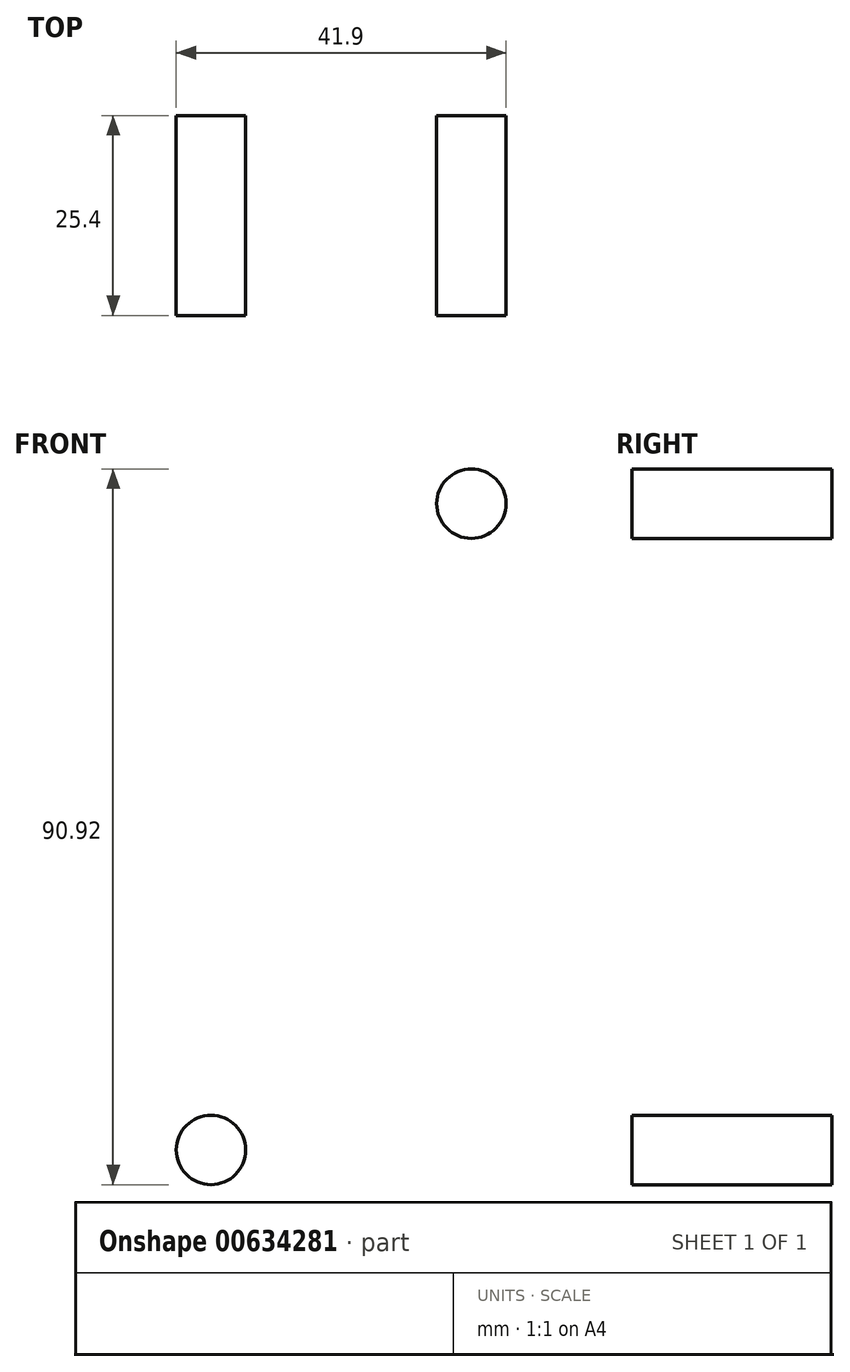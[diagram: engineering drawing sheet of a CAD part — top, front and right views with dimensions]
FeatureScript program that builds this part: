
annotation { "Feature Type Name" : "Feature", "Feature Type Description" : "" }
export const myFeature = defineFeature(function(context is Context, id is Id, definition is map)
    precondition{}
    {
        {
            var Q0;
            Q0=qCreatedBy(makeId("Front.planeOp"),FACE);
            var sketch = newSketch(context, id + "F0", { "sketchPlane" : qUnion([Q0])});
            skLineSegment(sketch, "E0.bottom", {"start": v(25.4, 50.8) * mm, "end": v(-25.4, 50.8) * mm});
            skLineSegment(sketch, "E0.top", {"start": v(25.4, -50.8) * mm, "end": v(-25.4, -50.8) * mm});
            skLineSegment(sketch, "E0.left", {"start": v(25.4, 50.8) * mm, "end": v(25.4, -50.8) * mm});
            skLineSegment(sketch, "E0.right", {"start": v(-25.4, 50.8) * mm, "end": v(-25.4, -50.8) * mm});
            skPoint(sketch, "E0.middle", {"position": v(0, 0) * mm});
            skCircle(sketch, "E1", {"center": v(0, -22.18) * mm, "radius": 7.62 * mm});
            skPoint(sketch, "E1.centerSnap0", {"position": v(0, -50.8) * mm});
            skCircle(sketch, "E2.MirrorC", {"center": v(0, 22.18) * mm, "radius": 7.62 * mm});
            skSolve(sketch);
        }
        {
            var Q0;
            Q0=makeQuery(id+"F0.imprint","IMPRINT",FACE,{"disambiguationData":[TD([[makeQuery(id+"F0.imprint","IMPRINT",EDGE,{"derivedFrom":sQuery(id+"F0.wireOp",EDGE,"E0.bottom")}),1.0]])]});
            extrude(context, id + "F1", {"entities" : qUnion([Q0]), "endBound" : BoundingType.SYMMETRIC, "depth" : 25.4 * mm, "offsetDistance" : 25.4 * mm});
        }
        {
            var Q0;
            Q0=makeQuery(id+"F1.opExtrude","SWEPT_EDGE",EDGE,{"disambiguationData":[OSD([sQuery(id+"F0.wireOp",EDGE,"E0.bottom"),sQuery(id+"F0.wireOp",EDGE,"E0.right")])]});
            var Q1;
            Q1=makeQuery(id+"F1.opExtrude","SWEPT_EDGE",EDGE,{"disambiguationData":[OSD([sQuery(id+"F0.wireOp",EDGE,"E0.bottom"),sQuery(id+"F0.wireOp",EDGE,"E0.left")])]});
            var Q2;
            Q2=makeQuery(id+"F1.opExtrude","SWEPT_EDGE",EDGE,{"disambiguationData":[OSD([sQuery(id+"F0.wireOp",EDGE,"E0.top"),sQuery(id+"F0.wireOp",EDGE,"E0.left")])]});
            var Q3;
            Q3=makeQuery(id+"F1.opExtrude","SWEPT_EDGE",EDGE,{"disambiguationData":[OSD([sQuery(id+"F0.wireOp",EDGE,"E0.top"),sQuery(id+"F0.wireOp",EDGE,"E0.right")])]});
            fillet(context, id + "F2", {"entities" : qUnion([Q0, Q1, Q2, Q3]), "radius" : 5.08 * mm, "tangentPropagation" : true, "allowEdgeOverflow" : false});
        }
        {
            var Q0;
            Q0=makeQuery(id+"F1.opExtrude","CAP_FACE",FACE,{"disambiguationData":[OSD([sQuery(id+"F0.wireOp",EDGE,"E0.bottom"),sQuery(id+"F0.wireOp",EDGE,"E0.top"),sQuery(id+"F0.wireOp",EDGE,"E0.left"),sQuery(id+"F0.wireOp",EDGE,"E0.right"),sQuery(id+"F0.wireOp",EDGE,"E1"),sQuery(id+"F0.wireOp",EDGE,"E2.MirrorC")])],"isStart":false});
            var sketch = newSketch(context, id + "F3", { "sketchPlane" : qUnion([Q0])});
            skCircle(sketch, "E3", {"center": v(-16.54, 41.05) * mm, "radius": 4.4 * mm});
            skCircle(sketch, "E4.MirrorC", {"center": v(16.54, 41.05) * mm, "radius": 4.4 * mm});
            skCircle(sketch, "E5.MirrorC", {"center": v(-16.54, -41.05) * mm, "radius": 4.4 * mm});
            skCircle(sketch, "E6.MirrorC", {"center": v(16.54, -41.05) * mm, "radius": 4.4 * mm});
            skSolve(sketch);
        }
        {
            var Q0;
            Q0=makeQuery(id+"F3.imprint","IMPRINT",FACE,{"disambiguationData":[TD([[makeQuery(id+"F3.imprint","IMPRINT",EDGE,{"derivedFrom":sQuery(id+"F3.wireOp",EDGE,"E3")}),1.0]])]});
            var Q1;
            Q1=makeQuery(id+"F3.imprint","IMPRINT",FACE,{"disambiguationData":[TD([[makeQuery(id+"F3.imprint","IMPRINT",EDGE,{"derivedFrom":sQuery(id+"F3.wireOp",EDGE,"E4.MirrorC")}),-1.0]])]});
            var Q2;
            Q2=makeQuery(id+"F3.imprint","IMPRINT",FACE,{"disambiguationData":[TD([[makeQuery(id+"F3.imprint","IMPRINT",EDGE,{"derivedFrom":sQuery(id+"F3.wireOp",EDGE,"E6.MirrorC")}),1.0]])]});
            var Q3;
            Q3=makeQuery(id+"F3.imprint","IMPRINT",FACE,{"disambiguationData":[TD([[makeQuery(id+"F3.imprint","IMPRINT",EDGE,{"derivedFrom":sQuery(id+"F3.wireOp",EDGE,"E5.MirrorC")}),-1.0]])]});
            extrude(context, id + "F4", {"entities" : qUnion([Q0, Q1, Q2, Q3]), "operationType" : NewBodyOperationType.REMOVE, "endBound" : BoundingType.THROUGH_ALL, "oppositeDirection" : true, "depth" : 25.4 * mm, "offsetDistance" : 25.4 * mm});
        }
    });
